# Revit family: ShowerHead-HandshowerSet-SoloC-Vitra-ShowerSystem-A45675
name_source: partatom
category: Plumbing Fixtures
revit_build: Autodesk Revit 2017 (Build: 20160225_1515(x64)
units: mm (PartAtom-declared; Revit-internal decimal feet)

## family parameters
Cut with Voids When Loaded = No
Host = Face
OmniClass Number = 23.45.55.17
OmniClass Title = Mixing Faucets
Part Type = Normal
Room Calculation Point = No
Round Connector Dimension = Use Diameter
Shared = Yes

## types (6) — shared parameters
BIMobject category = Bath/Shower Mixer
CW Connection = No
Coating Material = Chrome
Color = Chrome
Connection Diameter (mm) = 20 mm  [stored 0.0656168 ft]
Depth(mm) = 128 mm
Description = Solo C Handshower Set
Design country = Turkey
HW Connection = No
Height(mm) = 65 mm  [stored 0.213255 ft]
IFC Classification = Sanitary Terminal
Manufacturer = Vitra
Manufacturer name = Vitra
Masterformat 2014 Code = 22 41 23
Masterformat 2014 Description = Residential Showers
MountingType = Wall-mounted (exposed part)
NBS Referans Code = 35-06-81
NBS Referans Description = Shower Heads
Nominal height = 0.000
Nominal width = 0.000
Number Of Connections = 1 mm  [stored 0.00328084 ft]
OmniClass Code = 23-31 17 19
OmniClass Description = Shower Head Fixtures
Product Type = Showerhead
Product certification = https://vitraglobal.com
Product data url = https://www.vitraglobal.com
Product family = Shower System
Product group = HandshowerSet
Range of flow pressure = 0.5-10 bar (Recommended 3-5 Bars)
Technical description = https://www.vitraglobal.com
UNSPSC Code = 30181503
URL = https://vitraglobal.com
Uniclass 1.4 Code = L7214
Uniclass 1.4 Description = Showers
Uniclass 2.0 Code = PR-35-06-81
Uniclass 2.0 Description = Shower Heads
Uniclass 2015 Code = Pr_40_20_87_76
Uniclass 2015 Name = Shower heads
Uniformat II Code = D2010
Uniformat II Description = Plumbing Fixtures
Vent Connection = No
Warranty Period (Year) = 5 Years
Waste Connection = No
Weight Net (kg) = 0,980
Width(mm) = 245 mm  [stored 0.803806 ft]
Youtube = https://www.youtube.com
zero-valued in all types: CWFU, Cost, Default Elevation, HWFU, WFU

## per-type parameters (varying)
| type | Article No. (default) | Model | Product SKU |
| ShowerHead-HandshowerSet-SoloC-Vitra-ShowerSystem-A45675 | A45675 | A45675 | A45675 |
| ShowerHead-HandshowerSet-SoloC-Vitra-ShowerSystem-A45675EXP | A45675EXP | A45675EXP | A45675EXP |
| ShowerHead-HandshowerSet-SoloC-Vitra-ShowerSystem-A45675IND | A45675IND | A45675IND | A45675IND |
| ShowerHead-HandshowerSet-SoloC-Vitra-ShowerSystem-A45675TPL | A45675TPL | A45675TPL | A45675TPL |
| ShowerHead-HandshowerSet-SoloC-Vitra-ShowerSystem-A45675TPX | A45675TPX | A45675TPX | A45675TPX |
| ShowerHead-HandshowerSet-SoloC-Vitra-ShowerSystem-A45675WSA | A45675WSA | A45675WSA | A45675WSA |

note: [stored X ft] marks values corroborated as IEEE doubles in the binary element streams (Revit-internal decimal feet)

## geometry (parser evidence)
native form markers: Sweep x3
no freeform markers — native parametric forms only
